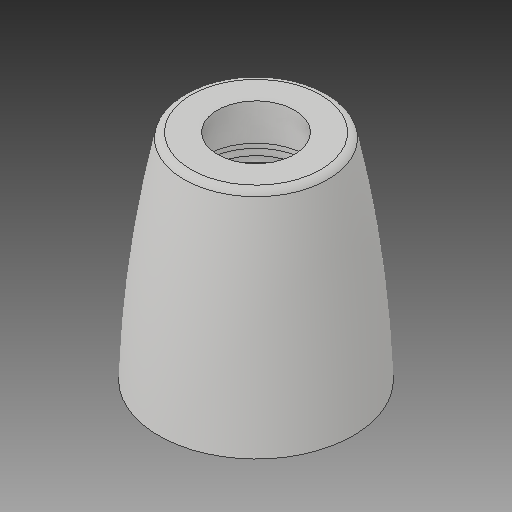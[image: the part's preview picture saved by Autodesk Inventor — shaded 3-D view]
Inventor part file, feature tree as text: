
AUTODESK INVENTOR PART (.ipt)
format: ipt  version: 2017 (Build 210142000, 142)  size: 146,944 bytes
history: native  units: in
note: dims shown in document units (in); Inventor stores cm internally (conversion verified against a paired STEP export)
features: revolve x1
ambient origin geometry x8: Origin, YZ Plane, XZ Plane, XY Plane, X Axis, Y Axis, Z Axis, Center Point
bodies: Solid1 (feature_tree)
feature tree (1):
  revolve  "Revolve1"  [1 undecoded]
note: 1 required parameter value undecoded (feature->parameter linkage not recoverable at this tier; creation-order binding heuristic only, values carry confidence <= 0.55)
